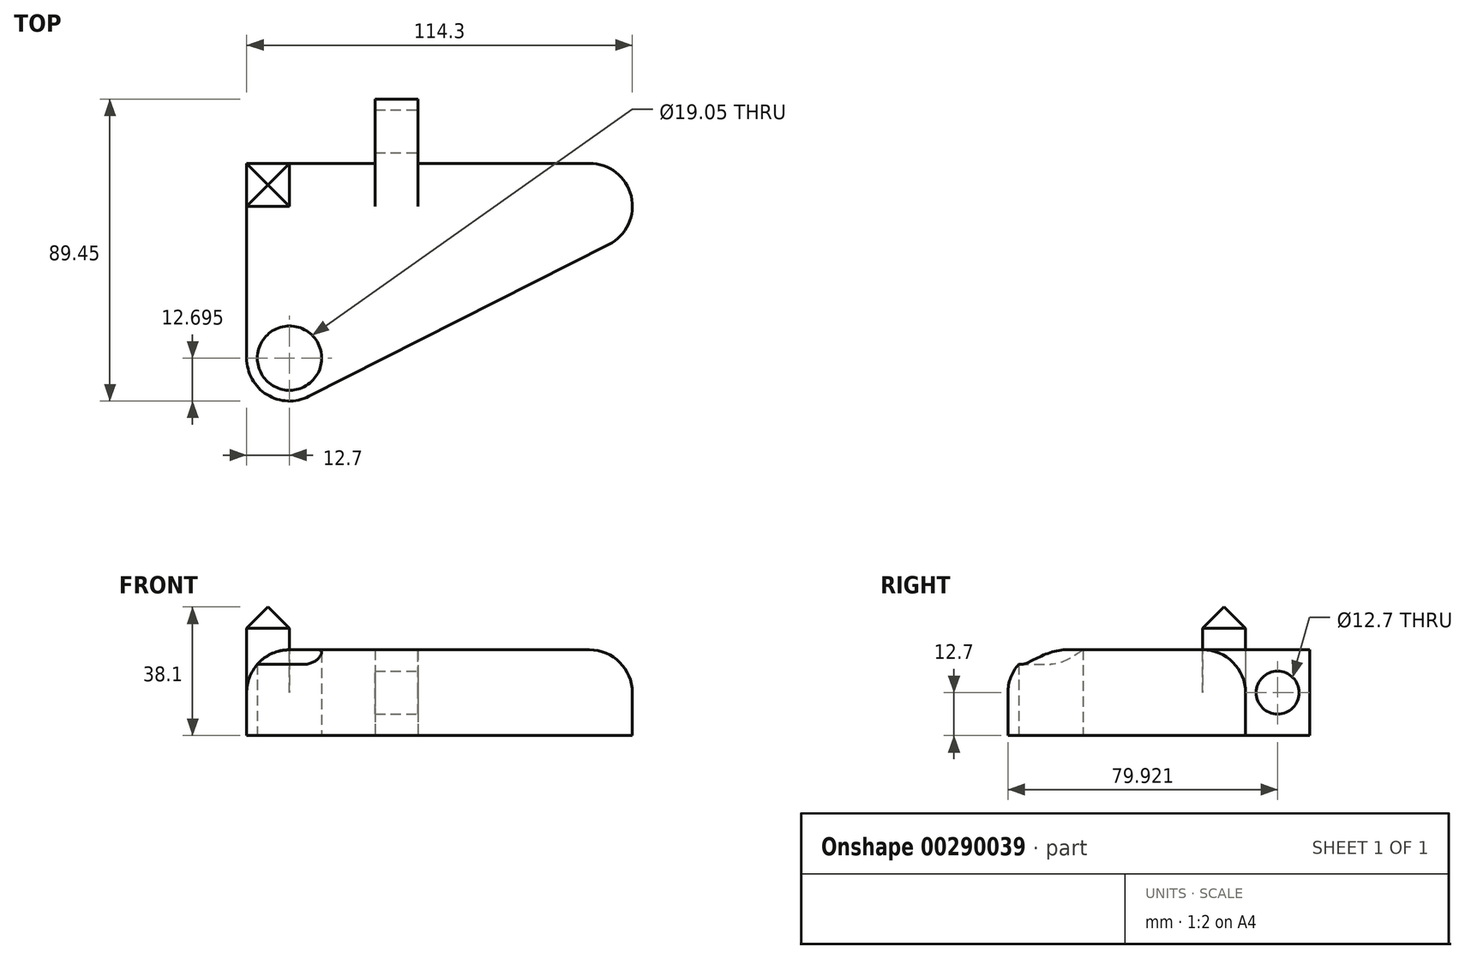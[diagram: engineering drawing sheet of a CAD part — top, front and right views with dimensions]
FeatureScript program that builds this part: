
annotation { "Feature Type Name" : "Feature", "Feature Type Description" : "" }
export const myFeature = defineFeature(function(context is Context, id is Id, definition is map)
    precondition{}
    {
        {
            var Q0;
            Q0=qCreatedBy(makeId("Top.planeOp"),FACE);
            var sketch = newSketch(context, id + "F0", { "sketchPlane" : qUnion([Q0])});
            skLineSegment(sketch, "E0.bottom", {"start": v(-44.57, 41.77) * mm, "end": v(-6.47, 41.77) * mm});
            skLineSegment(sketch, "E0.left", {"start": v(-44.57, 41.77) * mm, "end": v(-44.57, -15.93) * mm});
            skArc(sketch, "E1", {"start": v(62.77, 17.74) * mm, "mid": v(69.38, 32.01) * mm, "end": v(57.03, 41.77) * mm});
            skCircle(sketch, "E2", {"center": v(-31.87, -15.93) * mm, "radius": 12.7 * mm});
            skLineSegment(sketch, "E3", {"start": v(-26.13, -27.27) * mm, "end": v(62.77, 17.74) * mm});
            skLineSegment(sketch, "E4.top", {"start": v(-44.57, 29.07) * mm, "end": v(-31.87, 29.07) * mm});
            skLineSegment(sketch, "E4.right", {"start": v(-31.87, 41.77) * mm, "end": v(-31.87, 29.07) * mm});
            skLineSegment(sketch, "E5", {"start": v(-6.47, 41.77) * mm, "end": v(-6.47, 60.82) * mm});
            skLineSegment(sketch, "E6", {"start": v(-6.47, 60.82) * mm, "end": v(6.23, 60.82) * mm});
            skLineSegment(sketch, "E7", {"start": v(6.23, 60.82) * mm, "end": v(6.23, 41.77) * mm});
            skLineSegment(sketch, "E8.trimOffspring", {"start": v(6.23, 41.77) * mm, "end": v(57.03, 41.77) * mm});
            skCircle(sketch, "E9", {"center": v(-31.87, -15.93) * mm, "radius": 9.53 * mm});
            skSolve(sketch);
        }
        {
            var Q0;
            Q0 = qSketchRegion(id + "F0", true);
            extrude(context, id + "F1", {"entities" : qUnion([Q0]), "depth" : 25.4 * mm});
        }
        {
            var Q0;
            {var subQ4=sQuery(id+"F0.wireOp",EDGE,"E4.top");Q0=makeQuery(id+"F0.imprint","IMPRINT",FACE,{"disambiguationData":[TD([[makeQuery(id+"F0.imprint","IMPRINT",EDGE,{"derivedFrom":subQ4}),1.0]])]});}
            extrude(context, id + "F2", {"entities" : qUnion([Q0]), "operationType" : NewBodyOperationType.ADD, "depth" : 38.1 * mm});
        }
        {
            var Q0;
            Q0=makeQuery(id+"F2.opExtrude","CAP_EDGE",EDGE,{"disambiguationData":[OSD([sQuery(id+"F0.wireOp",EDGE,"E4.top")])],"isStart":false});
            var Q1;
            Q1=makeQuery(id+"F2.opExtrude","CAP_EDGE",EDGE,{"disambiguationData":[OSD([sQuery(id+"F0.wireOp",EDGE,"E0.left")])],"isStart":false});
            var Q2;
            Q2=makeQuery(id+"F2.opExtrude","CAP_EDGE",EDGE,{"disambiguationData":[OSD([sQuery(id+"F0.wireOp",EDGE,"E0.bottom")])],"isStart":false});
            var Q3;
            Q3=makeQuery(id+"F2.opExtrude","CAP_EDGE",EDGE,{"disambiguationData":[OSD([sQuery(id+"F0.wireOp",EDGE,"E4.right")])],"isStart":false});
            chamfer(context, id + "F3", {"entities" : qUnion([Q0, Q1, Q2, Q3]), "width" : 6.35 * mm, "tangentPropagation" : true});
        }
        {
            var Q0;
            Q0=makeQuery(id+"F1.opExtrude","CAP_EDGE",EDGE,{"disambiguationData":[OSD([sQuery(id+"F0.wireOp",EDGE,"E8.trimOffspring")])],"isStart":false});
            var Q1;
            Q1=makeQuery(id+"F1.opExtrude","CAP_EDGE",EDGE,{"disambiguationData":[OSD([sQuery(id+"F0.wireOp",EDGE,"E1")])],"isStart":false});
            var Q2;
            Q2=makeQuery(id+"F1.opExtrude","CAP_EDGE",EDGE,{"disambiguationData":[OSD([sQuery(id+"F0.wireOp",EDGE,"E3")])],"isStart":false});
            var Q3;
            Q3=makeQuery(id+"F1.opExtrude","CAP_EDGE",EDGE,{"disambiguationData":[OSD([sQuery(id+"F0.wireOp",EDGE,"E0.bottom")])],"isStart":false});
            var Q4;
            Q4=makeQuery(id+"F1.opExtrude","CAP_EDGE",EDGE,{"disambiguationData":[OSD([sQuery(id+"F0.wireOp",EDGE,"E0.left")])],"isStart":false});
            var Q5;
            Q5=makeQuery(id+"F1.opExtrude","CAP_EDGE",EDGE,{"disambiguationData":[OSD([sQuery(id+"F0.wireOp",EDGE,"E2")])],"isStart":false});
            fillet(context, id + "F4", {"entities" : qUnion([Q0, Q1, Q2, Q3, Q4, Q5]), "radius" : 12.7 * mm, "tangentPropagation" : true, "allowEdgeOverflow" : false});
        }
        {
            var Q0;
            Q0=makeQuery(id+"F1.opExtrude","SWEPT_FACE",FACE,{"disambiguationData":[OSD([sQuery(id+"F0.wireOp",EDGE,"E7")])]});
            var sketch = newSketch(context, id + "F5", { "sketchPlane" : qUnion([Q0])});
            skLineSegment(sketch, "E10", {"start": v(60.82, 12.7) * mm, "end": v(41.77, 12.7) * mm, "construction": true});
            skLineSegment(sketch, "E11", {"start": v(51.3, 25.4) * mm, "end": v(51.3, 0) * mm, "construction": true});
            skPoint(sketch, "E12.orphan", {"position": v(51.3, 12.7) * mm});
            skCircle(sketch, "E13", {"center": v(51.3, 12.7) * mm, "radius": 6.35 * mm});
            skSolve(sketch);
        }
        {
            var Q0;
            Q0=makeQuery(id+"F5.imprint","IMPRINT",FACE,{"disambiguationData":[TD([[makeQuery(id+"F5.imprint","IMPRINT",EDGE,{"derivedFrom":sQuery(id+"F5.wireOp",EDGE,"E13")}),1.0]])]});
            var Q1;
            Q1=sQuery(id+"F5.wireOp",EDGE,"E13");
            extrude(context, id + "F6", {"entities" : qUnion([Q0]), "operationType" : NewBodyOperationType.REMOVE, "surfaceEntities" : qUnion([Q1]), "endBound" : BoundingType.THROUGH_ALL, "oppositeDirection" : true, "depth" : 25.4 * mm});
        }
    });
